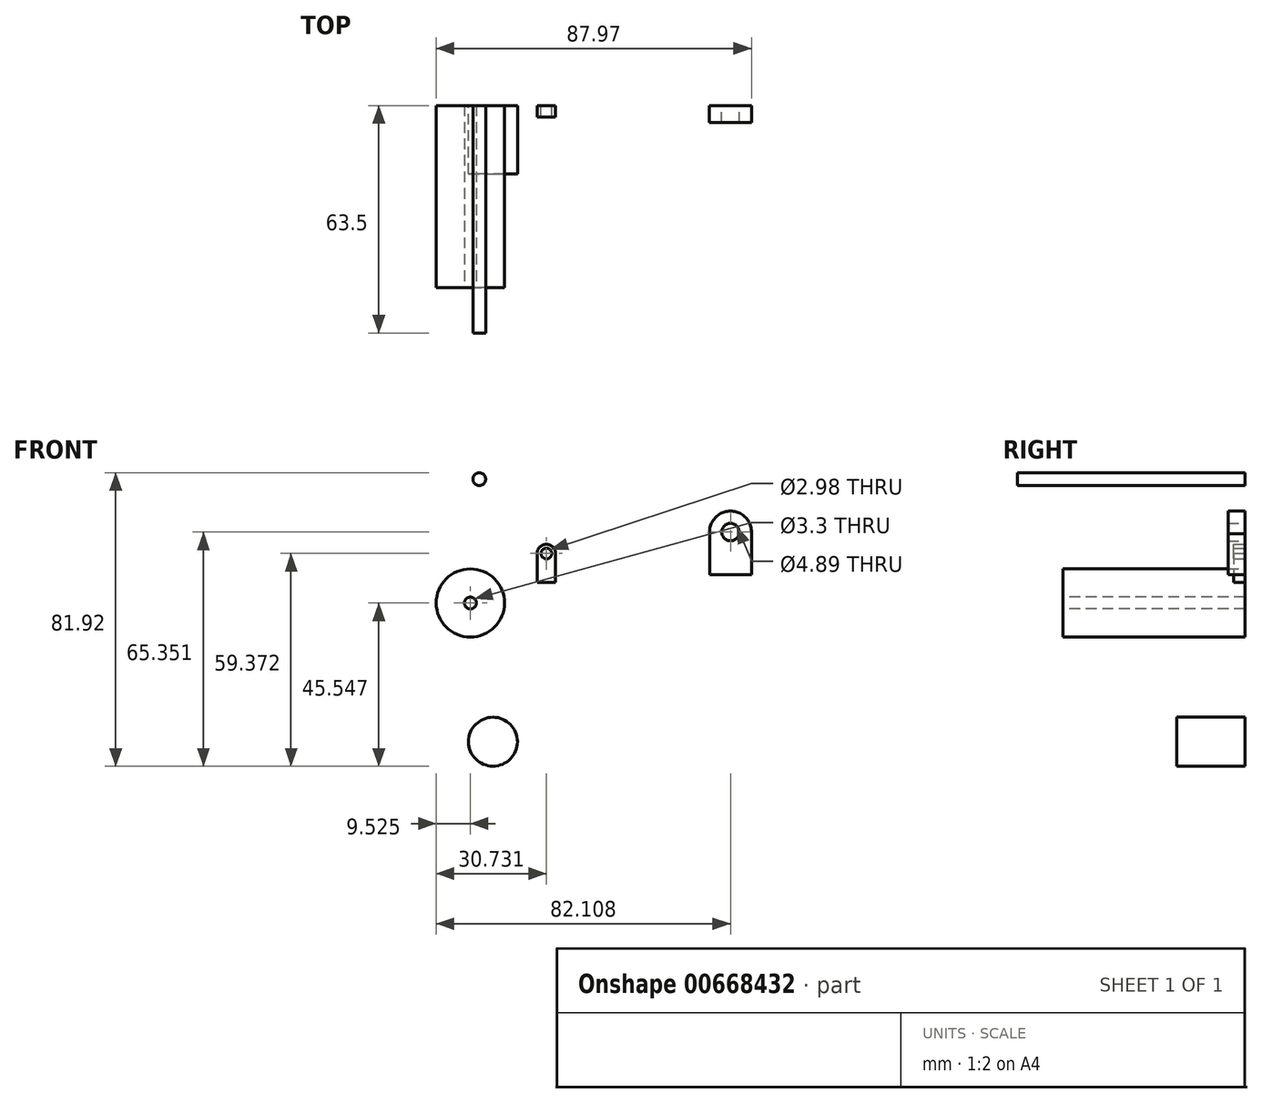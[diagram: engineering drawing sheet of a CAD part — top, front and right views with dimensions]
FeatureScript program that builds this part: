
annotation { "Feature Type Name" : "Feature", "Feature Type Description" : "" }
export const myFeature = defineFeature(function(context is Context, id is Id, definition is map)
    precondition{}
    {
        {
            var Q0;
            Q0=qCreatedBy(makeId("Front.planeOp"),FACE);
            var sketch = newSketch(context, id + "F0", { "sketchPlane" : qUnion([Q0])});
            skCircle(sketch, "E0", {"center": v(-41.99, 12.48) * mm, "radius": 9.53 * mm});
            skSolve(sketch);
        }
        {
            var Q0;
            Q0=makeQuery(id+"F0.imprint","IMPRINT",FACE,{"disambiguationData":[TD([[makeQuery(id+"F0.imprint","IMPRINT",EDGE,{"derivedFrom":sQuery(id+"F0.wireOp",EDGE,"E0")}),1.0]])]});
            extrude(context, id + "F1", {"entities" : qUnion([Q0]), "depth" : 50.8 * mm});
        }
        {
            var Q0;
            Q0=makeQuery(id+"F1.opExtrude","CAP_FACE",FACE,{"disambiguationData":[OSD([sQuery(id+"F0.wireOp",EDGE,"E0")])],"isStart":false});
            var sketch = newSketch(context, id + "F2", { "sketchPlane" : qUnion([Q0])});
            skCircle(sketch, "E1", {"center": v(-41.99, 12.48) * mm, "radius": 5.4 * mm});
            skSolve(sketch);
        }
        {
            var Q0;
            Q0=sQuery(id+"F2.wireOp",VERTEX,"E1.center");
            var Q1;
            Q1=makeQuery(id+"F1.opExtrude","SWEPT_BODY",BODY,{"disambiguationData":[OSD([sQuery(id+"F0.wireOp",EDGE,"E0")])]});
            hole(context, id + "F3", {"style" : HoleStyle.SIMPLE, "endStyle" : HoleEndStyle.THROUGH, "standardTappedOrClearance" : lookupTablePath({ "standard" : "ISO", "fit" : "Normal", "size" : "M3", "type" : "Clearance" }), "standardBlindInLast" : lookupTablePath({ "fit" : "Standard", "standard" : "ISO", "size" : "M3", "type" : "Clearance" }), "holeDiameter" : 3.3 * mm, "isTappedThrough" : true, "tappedDepth" : 12.7 * mm, "tapClearance" : 3, "locations" : qUnion([Q0]), "scope" : qUnion([Q1])});
        }
        {
            var Q0;
            Q0=qCreatedBy(makeId("Front.planeOp"),FACE);
            var sketch = newSketch(context, id + "F4", { "sketchPlane" : qUnion([Q0])});
            skCircle(sketch, "E2", {"center": v(-39.51, 47.06) * mm, "radius": 1.79 * mm});
            skSolve(sketch);
        }
        {
            var Q0;
            Q0=makeQuery(id+"F4.imprint","IMPRINT",FACE,{"disambiguationData":[TD([[makeQuery(id+"F4.imprint","IMPRINT",EDGE,{"derivedFrom":sQuery(id+"F4.wireOp",EDGE,"E2")}),1.0]])]});
            extrude(context, id + "F5", {"entities" : qUnion([Q0]), "depth" : 63.5 * mm});
        }
        {
            var Q0;
            Q0=qCreatedBy(makeId("Front.planeOp"),FACE);
            var sketch = newSketch(context, id + "F6", { "sketchPlane" : qUnion([Q0])});
            skCircle(sketch, "E3", {"center": v(-35.68, -26.24) * mm, "radius": 6.83 * mm});
            skSolve(sketch);
        }
        {
            var Q0;
            Q0=makeQuery(id+"F6.imprint","IMPRINT",FACE,{"disambiguationData":[TD([[makeQuery(id+"F6.imprint","IMPRINT",EDGE,{"derivedFrom":sQuery(id+"F6.wireOp",EDGE,"E3")}),1.0]])]});
            extrude(context, id + "F7", {"entities" : qUnion([Q0]), "depth" : 19.05 * mm});
        }
        {
            var Q0;
            Q0=qCreatedBy(makeId("Front.planeOp"),FACE);
            var sketch = newSketch(context, id + "F8", { "sketchPlane" : qUnion([Q0])});
            skLineSegment(sketch, "E4.top", {"start": v(24.76, 20.4) * mm, "end": v(36.44, 20.4) * mm});
            skLineSegment(sketch, "E4.left", {"start": v(24.76, 32.28) * mm, "end": v(24.76, 20.4) * mm});
            skLineSegment(sketch, "E4.right", {"start": v(36.44, 32.28) * mm, "end": v(36.44, 20.4) * mm});
            skArc(sketch, "E5", {"start": v(36.44, 31.79) * mm, "mid": v(30.6, 38.14) * mm, "end": v(24.76, 31.79) * mm});
            skCircle(sketch, "E6", {"center": v(30.6, 32.28) * mm, "radius": 2.45 * mm});
            skSolve(sketch);
        }
        {
            var Q0;
            {var subQ2=sQuery(id+"F8.wireOp",EDGE,"E4.top");Q0=makeQuery(id+"F8.imprint","IMPRINT",FACE,{"disambiguationData":[TD([[makeQuery(id+"F8.imprint","IMPRINT",EDGE,{"derivedFrom":subQ2}),1.0]])]});}
            extrude(context, id + "F9", {"entities" : qUnion([Q0]), "depth" : 4.75 * mm});
        }
        {
            var Q0;
            Q0=qCreatedBy(makeId("Front.planeOp"),FACE);
            var sketch = newSketch(context, id + "F10", { "sketchPlane" : qUnion([Q0])});
            skLineSegment(sketch, "E7.bottom", {"start": v(-23.36, 26.3) * mm, "end": v(-23.36, 26.3) * mm});
            skLineSegment(sketch, "E7.top", {"start": v(-23.36, 18.29) * mm, "end": v(-18.2, 18.29) * mm});
            skLineSegment(sketch, "E7.left", {"start": v(-23.36, 26.3) * mm, "end": v(-23.36, 18.29) * mm});
            skLineSegment(sketch, "E7.right", {"start": v(-18.2, 26.3) * mm, "end": v(-18.2, 18.29) * mm});
            skArc(sketch, "E8", {"start": v(-18.2, 26.3) * mm, "mid": v(-20.78, 28.88) * mm, "end": v(-23.36, 26.3) * mm});
            skLineSegment(sketch, "E9.trimOffspring", {"start": v(-18.2, 26.3) * mm, "end": v(-18.2, 26.3) * mm});
            skCircle(sketch, "E10", {"center": v(-20.78, 26.3) * mm, "radius": 1.5 * mm});
            skSolve(sketch);
        }
        {
            var Q0;
            Q0=makeQuery(id+"F10.imprint","IMPRINT",FACE,{"disambiguationData":[TD([[makeQuery(id+"F10.imprint","IMPRINT",EDGE,{"derivedFrom":sQuery(id+"F10.wireOp",EDGE,"E7.bottom")}),-1.0]])]});
            extrude(context, id + "F11", {"entities" : qUnion([Q0]), "depth" : 3.17 * mm});
        }
    });
